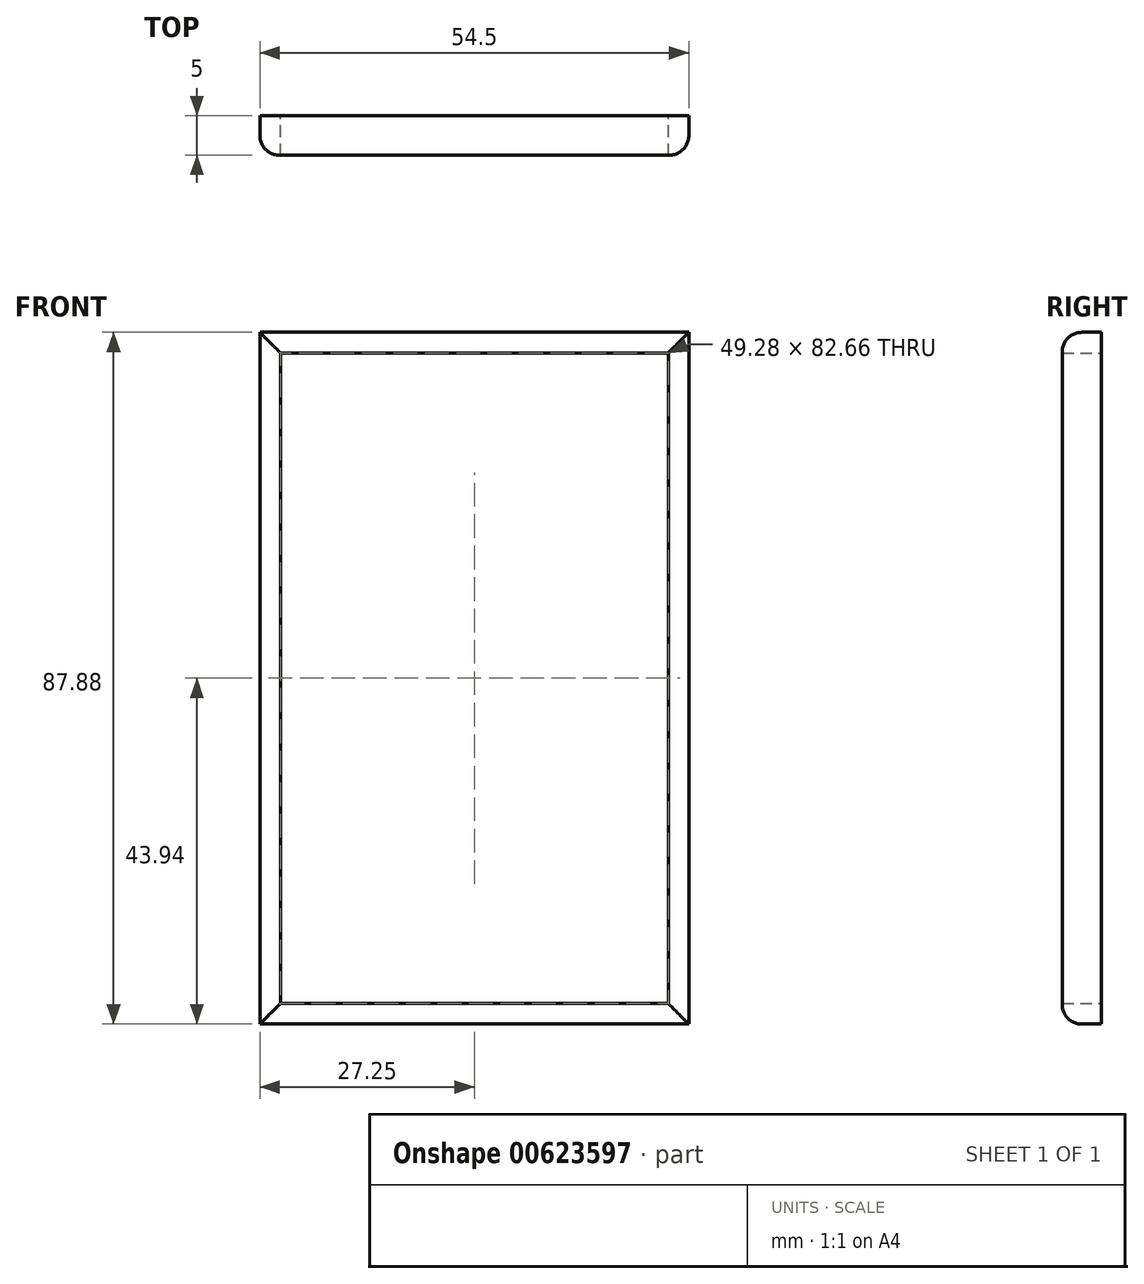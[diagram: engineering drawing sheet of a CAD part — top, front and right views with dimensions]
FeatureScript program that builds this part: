
annotation { "Feature Type Name" : "Feature", "Feature Type Description" : "" }
export const myFeature = defineFeature(function(context is Context, id is Id, definition is map)
    precondition{}
    {
        {
            var Q0;
            Q0=qCreatedBy(makeId("Front.planeOp"),FACE);
            var sketch = newSketch(context, id + "F0", { "sketchPlane" : qUnion([Q0])});
            skLineSegment(sketch, "E0.bottom", {"start": v(27.25, 43.94) * mm, "end": v(-27.25, 43.94) * mm});
            skLineSegment(sketch, "E0.top", {"start": v(27.25, -43.94) * mm, "end": v(-27.25, -43.94) * mm});
            skLineSegment(sketch, "E0.left", {"start": v(27.25, 43.94) * mm, "end": v(27.25, -43.94) * mm});
            skLineSegment(sketch, "E0.right", {"start": v(-27.25, 43.94) * mm, "end": v(-27.25, -43.94) * mm});
            skPoint(sketch, "E0.middle", {"position": v(0, 0) * mm});
            skLineSegment(sketch, "E1.bottom", {"start": v(24.64, 41.33) * mm, "end": v(-24.64, 41.33) * mm});
            skLineSegment(sketch, "E1.top", {"start": v(24.64, -41.33) * mm, "end": v(-24.64, -41.33) * mm});
            skLineSegment(sketch, "E1.left", {"start": v(24.64, 41.33) * mm, "end": v(24.64, -41.33) * mm});
            skLineSegment(sketch, "E1.right", {"start": v(-24.64, 41.33) * mm, "end": v(-24.64, -41.33) * mm});
            skSolve(sketch);
        }
        {
            var Q0;
            Q0=makeQuery(id+"F0.imprint","IMPRINT",FACE,{"disambiguationData":[TD([[makeQuery(id+"F0.imprint","IMPRINT",EDGE,{"derivedFrom":sQuery(id+"F0.wireOp",EDGE,"E0.bottom")}),1.0]])]});
            extrude(context, id + "F1", {"entities" : qUnion([Q0]), "depth" : 5 * mm, "offsetDistance" : 25 * mm});
        }
        {
            var Q0;
            Q0=makeQuery(id+"F1.opExtrude","CAP_EDGE",EDGE,{"disambiguationData":[OSD([sQuery(id+"F0.wireOp",EDGE,"E0.left")])],"isStart":false});
            var Q1;
            Q1=makeQuery(id+"F1.opExtrude","CAP_EDGE",EDGE,{"disambiguationData":[OSD([sQuery(id+"F0.wireOp",EDGE,"E0.bottom")])],"isStart":false});
            var Q2;
            Q2=makeQuery(id+"F1.opExtrude","CAP_EDGE",EDGE,{"disambiguationData":[OSD([sQuery(id+"F0.wireOp",EDGE,"E0.right")])],"isStart":false});
            var Q3;
            Q3=makeQuery(id+"F1.opExtrude","CAP_EDGE",EDGE,{"disambiguationData":[OSD([sQuery(id+"F0.wireOp",EDGE,"E0.top")])],"isStart":false});
            fillet(context, id + "F2", {"entities" : qUnion([Q0, Q1, Q2, Q3]), "radius" : 2.5 * mm, "tangentPropagation" : true, "allowEdgeOverflow" : false});
        }
    });
